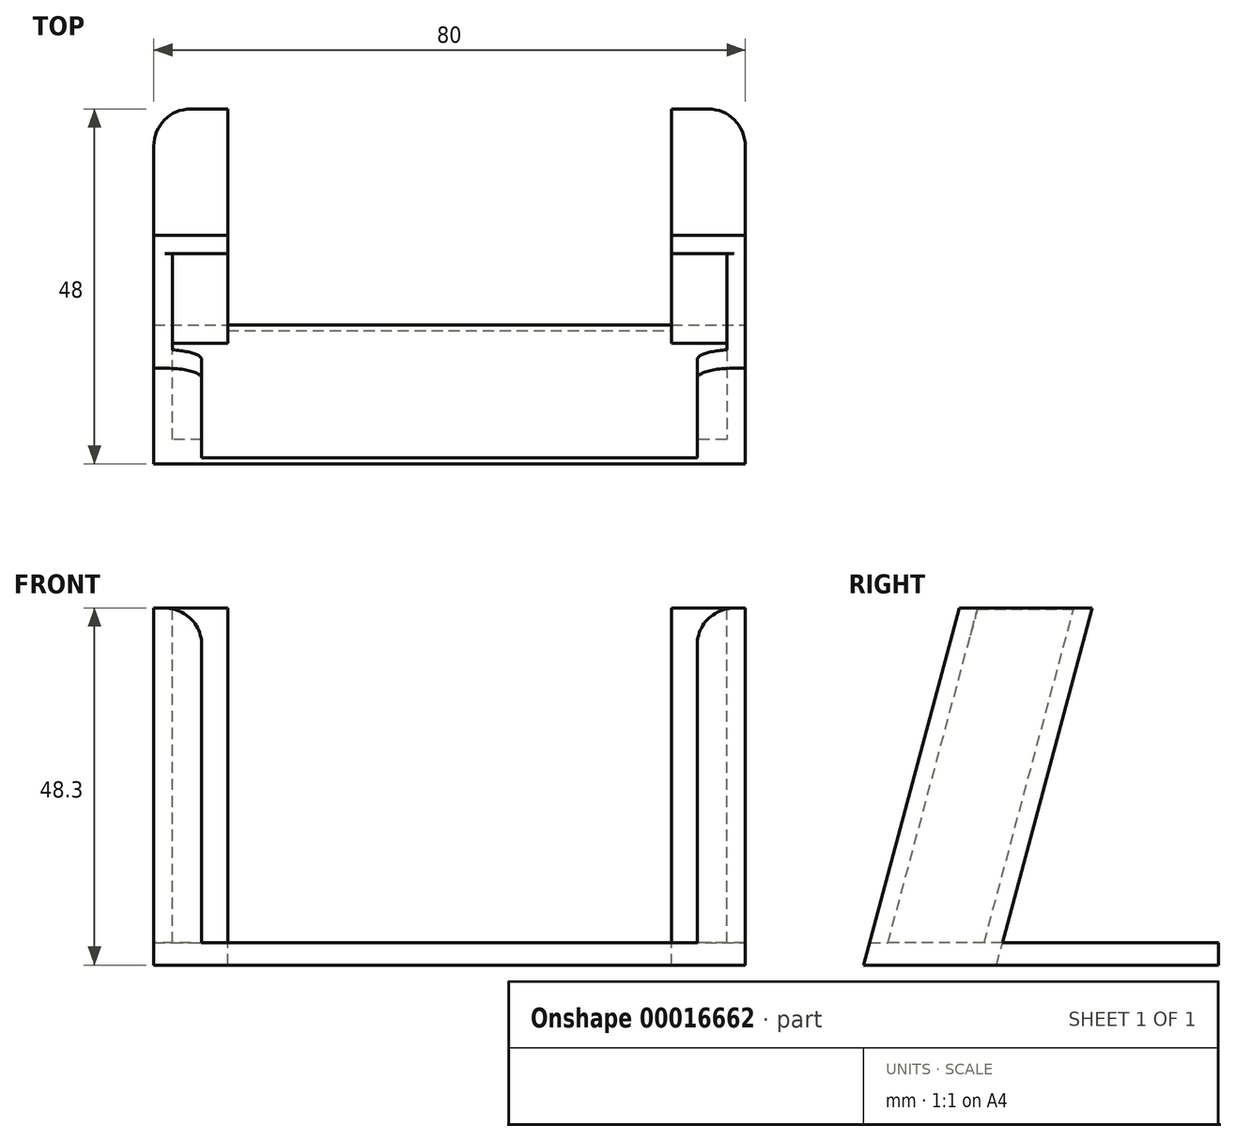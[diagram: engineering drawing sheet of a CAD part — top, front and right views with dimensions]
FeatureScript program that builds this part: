
annotation { "Feature Type Name" : "Feature", "Feature Type Description" : "" }
export const myFeature = defineFeature(function(context is Context, id is Id, definition is map)
    precondition{}
    {
        {
            var Q0;
            Q0=qCreatedBy(makeId("Top.planeOp"),FACE);
            var sketch = newSketch(context, id + "F0", { "sketchPlane" : qUnion([Q0])});
            skLineSegment(sketch, "E0.bottom", {"start": v(0, 0) * mm, "end": v(77.5, 0) * mm});
            skLineSegment(sketch, "E0.top", {"start": v(0, -18) * mm, "end": v(77.5, -18) * mm});
            skLineSegment(sketch, "E0.left", {"start": v(0, 0) * mm, "end": v(0, -18) * mm});
            skLineSegment(sketch, "E0.right", {"start": v(77.5, 0) * mm, "end": v(77.5, -18) * mm});
            skSolve(sketch);
        }
        {
            var Q0;
            Q0=makeQuery(id+"F0.imprint","IMPRINT",FACE,{"disambiguationData":[TD([[makeQuery(id+"F0.imprint","IMPRINT",EDGE,{"derivedFrom":sQuery(id+"F0.wireOp",EDGE,"E0.bottom")}),-1.0]])]});
            var sketch = newSketch(context, id + "F1", { "sketchPlane" : qUnion([Q0])});
            skLineSegment(sketch, "E1.bottom", {"start": v(0, 0) * mm, "end": v(10, 0) * mm});
            skLineSegment(sketch, "E1.top", {"start": v(0, -2.5) * mm, "end": v(10, -2.5) * mm});
            skLineSegment(sketch, "E1.left", {"start": v(0, 0) * mm, "end": v(0, -2.5) * mm});
            skLineSegment(sketch, "E1.right", {"start": v(10, 0) * mm, "end": v(10, -2.5) * mm});
            skLineSegment(sketch, "E2.bottom", {"start": v(0, -2.5) * mm, "end": v(2.5, -2.5) * mm});
            skLineSegment(sketch, "E2.top", {"start": v(0, -18) * mm, "end": v(2.5, -18) * mm});
            skLineSegment(sketch, "E2.left", {"start": v(0, -2.5) * mm, "end": v(0, -18) * mm});
            skLineSegment(sketch, "E2.right", {"start": v(2.5, -2.5) * mm, "end": v(2.5, -18) * mm});
            skLineSegment(sketch, "E3.bottom", {"start": v(2.5, -15.5) * mm, "end": v(6.5, -15.5) * mm});
            skLineSegment(sketch, "E3.top", {"start": v(2.5, -18) * mm, "end": v(6.5, -18) * mm});
            skLineSegment(sketch, "E3.left", {"start": v(2.5, -15.5) * mm, "end": v(2.5, -18) * mm});
            skLineSegment(sketch, "E3.right", {"start": v(6.5, -15.5) * mm, "end": v(6.5, -18) * mm});
            skLineSegment(sketch, "E4", {"start": v(40, 38.6) * mm, "end": v(40, -47.5) * mm});
            skLineSegment(sketch, "E5.0.MirrorCS", {"start": v(80, -2.5) * mm, "end": v(77.5, -2.5) * mm});
            skLineSegment(sketch, "E5.1.MirrorCS", {"start": v(80, -18) * mm, "end": v(77.5, -18) * mm});
            skLineSegment(sketch, "E5.2.MirrorCS", {"start": v(70, 0) * mm, "end": v(70, -2.5) * mm});
            skLineSegment(sketch, "E5.3.MirrorCS", {"start": v(80, 0) * mm, "end": v(80, -2.5) * mm});
            skLineSegment(sketch, "E5.4.MirrorCS", {"start": v(77.5, -15.5) * mm, "end": v(77.5, -18) * mm});
            skLineSegment(sketch, "E5.5.MirrorCS", {"start": v(73.5, -15.5) * mm, "end": v(73.5, -18) * mm});
            skLineSegment(sketch, "E5.6.MirrorCS", {"start": v(80, -2.5) * mm, "end": v(80, -18) * mm});
            skLineSegment(sketch, "E5.7.MirrorCS", {"start": v(80, 0) * mm, "end": v(70, 0) * mm});
            skLineSegment(sketch, "E5.8.MirrorCS", {"start": v(80, -2.5) * mm, "end": v(70, -2.5) * mm});
            skLineSegment(sketch, "E5.9.MirrorCS", {"start": v(77.5, -2.5) * mm, "end": v(77.5, -18) * mm});
            skLineSegment(sketch, "E5.10.MirrorCS", {"start": v(77.5, -18) * mm, "end": v(73.5, -18) * mm});
            skLineSegment(sketch, "E5.11.MirrorCS", {"start": v(77.5, -15.5) * mm, "end": v(73.5, -15.5) * mm});
            skSolve(sketch);
        }
        {
            var Q0;
            Q0=qCreatedBy(makeId("Right.planeOp"),FACE);
            var sketch = newSketch(context, id + "F2", { "sketchPlane" : qUnion([Q0])});
            skLineSegment(sketch, "E6", {"start": v(-20, 0) * mm, "end": v(-7.06, 48.3) * mm});
            skSolve(sketch);
        }
        {
            var Q0;
            Q0=qCreatedBy(makeId("Right.planeOp"),FACE);
            var sketch = newSketch(context, id + "F3", { "sketchPlane" : qUnion([Q0])});
            skLineSegment(sketch, "E7", {"start": v(0.8, 3) * mm, "end": v(0, 0) * mm});
            skSolve(sketch);
        }
        {
            var Q0;
            Q0 = qSketchRegion(id + "F0", true);
            var Q1;
            Q1 = qConstructionFilter(qBodyType(qCreatedBy(id + "F3" ,EDGE), BodyType.WIRE), ConstructionObject.NO);
            sweep(context, id + "F4", {"profiles" : qUnion([Q0]), "path" : qUnion([Q1])});
        }
        {
            var Q0;
            Q0 = qSketchRegion(id + "F1", true);
            var Q1;
            Q1 = qConstructionFilter(qBodyType(qCreatedBy(id + "F2" ,EDGE), BodyType.WIRE), ConstructionObject.NO);
            sweep(context, id + "F5", {"operationType" : NewBodyOperationType.ADD, "profiles" : qUnion([Q0]), "path" : qUnion([Q1])});
        }
        {
            var Q0;
            Q0=qCreatedBy(makeId("Right.planeOp"),FACE);
            cPlane(context, id + "F6", {"entities" : qUnion([Q0]), "cplaneType" : CPlaneType.OFFSET, "offset" : 40 * mm, "width" : 150 * mm, "height" : 150 * mm});
        }
        {
            var Q0;
            Q0=qCreatedBy(makeId("Top.planeOp"),FACE);
            var sketch = newSketch(context, id + "F7", { "sketchPlane" : qUnion([Q0])});
            skLineSegment(sketch, "E8.bottom", {"start": v(0, 0) * mm, "end": v(10, 0) * mm});
            skLineSegment(sketch, "E8.top", {"start": v(0, 30) * mm, "end": v(10, 30) * mm});
            skLineSegment(sketch, "E8.left", {"start": v(0, 0) * mm, "end": v(0, 30) * mm});
            skLineSegment(sketch, "E8.right", {"start": v(10, 0) * mm, "end": v(10, 30) * mm});
            skLineSegment(sketch, "E9.MirrorCS", {"start": v(80, 0) * mm, "end": v(80, 30) * mm});
            skLineSegment(sketch, "E10.MirrorCS", {"start": v(70, 0) * mm, "end": v(70, 30) * mm});
            skLineSegment(sketch, "E11.MirrorCS", {"start": v(80, 30) * mm, "end": v(70, 30) * mm});
            skLineSegment(sketch, "E12.MirrorCS", {"start": v(80, 0) * mm, "end": v(70, 0) * mm});
            skSolve(sketch);
        }
        {
            var Q0;
            Q0 = qSketchRegion(id + "F7", true);
            extrude(context, id + "F8", {"entities" : qUnion([Q0]), "operationType" : NewBodyOperationType.ADD, "depth" : 3 * mm});
        }
        {
            var Q0;
            Q0=makeQuery(id+"F8.opExtrude","SWEPT_EDGE",EDGE,{"disambiguationData":[OSD([sQuery(id+"F7.wireOp",EDGE,"E9.MirrorCS"),sQuery(id+"F7.wireOp",EDGE,"E11.MirrorCS")])]});
            fillet(context, id + "F9", {"entities" : qUnion([Q0]), "radius" : 5 * mm, "tangentPropagation" : true, "allowEdgeOverflow" : false});
        }
        {
            var Q0;
            Q0=makeQuery(id+"F8.opExtrude","SWEPT_EDGE",EDGE,{"disambiguationData":[OSD([sQuery(id+"F7.wireOp",EDGE,"E8.top"),sQuery(id+"F7.wireOp",EDGE,"E8.left")])]});
            fillet(context, id + "F10", {"entities" : qUnion([Q0]), "radius" : 5 * mm, "tangentPropagation" : true, "allowEdgeOverflow" : false});
        }
        {
            var Q0;
            Q0=makeQuery(id+"F5.opSweep","CAP_EDGE",EDGE,{"disambiguationData":[OSD([sQuery(id+"F1.wireOp",EDGE,"E3.right"),sQuery(id+"F2.wireOp",VERTEX,"E6.end")])],"isStart":false});
            fillet(context, id + "F11", {"entities" : qUnion([Q0]), "radius" : 5 * mm, "tangentPropagation" : true, "allowEdgeOverflow" : false});
        }
        {
            var Q0;
            Q0=makeQuery(id+"F5.opSweep","CAP_EDGE",EDGE,{"disambiguationData":[OSD([sQuery(id+"F1.wireOp",EDGE,"E5.5.MirrorCS"),sQuery(id+"F2.wireOp",VERTEX,"E6.end")])],"isStart":false});
            fillet(context, id + "F12", {"entities" : qUnion([Q0]), "radius" : 5 * mm, "tangentPropagation" : true, "allowEdgeOverflow" : false});
        }
    });
